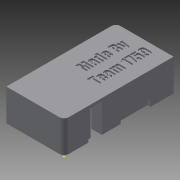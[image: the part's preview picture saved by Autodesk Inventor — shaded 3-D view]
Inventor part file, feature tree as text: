
AUTODESK INVENTOR PART (.ipt)
format: ipt  version: 2015 (Build 190159000, 159)  size: 555,008 bytes
history: native  units: in
note: dims shown in document units (in); Inventor stores cm internally (conversion verified against a paired STEP export)
features: extrude x10, sketch x9, projected_geometry x3, fillet x2
ambient origin geometry x8: Origin, YZ Plane, XZ Plane, XY Plane, X Axis, Y Axis, Z Axis, Center Point
bodies: Solid1 (feature_tree)
feature tree (24):
  extrude  "Extrusion1"  Depth=0.966in
  sketch  "Sketch2"  dims[d5=0.075in d6=0.1in d7=0.1in]
  fillet  "Fillet1"  Radius=0.533in
  fillet  "Fillet2"  Radius=0.075in
  extrude  "Extrusion2"  Depth=0.1in
  extrude  "Extrusion3"  Depth=0.125in
  extrude  "Extrusion4"  Depth=0.1in
  sketch  "Sketch6"  dims[d15=0.1in d16=0.1in]
  extrude  "Extrusion5"  Depth=0.1in
  sketch  "Sketch7"  dims[d17=0.1in d18=0.483in]
  extrude  "Extrusion7"  Depth=0.483in
  extrude  "Extrusion8"  Depth=0.1in
  extrude  "Extrusion9"  Depth=0.1in
  extrude  "Extrusion10"  Depth=0.5in
  extrude  "Extrusion11"  Depth=0.45in
  sketch  "Sketch1"  dims[d0=1.833in d1=0.966in d2=0.533in d3=0.0in d4=0.075in]
  sketch  "Sketch4"  dims[d8=0.1in d9=0.1in d11=0.125in]
  sketch  "Sketch5"  dims[d13=0.175in d14=0.1in]
  sketch  "Sketch8"  dims[d19=0.0in d20=0.1in]
  projected_geometry  "Projected Loop1"
  sketch  "Sketch9"  dims[d21=0.24in d22=0.1in]
  projected_geometry  "Projected Loop2"
  sketch  "Sketch10"  dims[d23=0.545in d24=0.5in d25=0.45in d26=0.9in d27=0.533in d28=0.0in d29=0.279in d30=0.185in d32=0.3in d33=0.1in d34=0.533in d35=0.0in d36=0.1718in d37=1.2625in d38=0.025in d39=0.0in d40=0.05in d41=0.1in d42=0.025in d43=0.025in d46=0.05in d47=0.025in d48=0.0in d49=0.025in d50=0.0in d51=0.1in d52=0.5in d53=0.05in d54=0.0in d55=0.1in d56=0.0in d57=1.0in d58=0.5in d59=0.025in d60=0.0in d61=0.375in]
  projected_geometry  "Projected Loop3"
